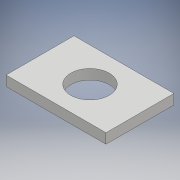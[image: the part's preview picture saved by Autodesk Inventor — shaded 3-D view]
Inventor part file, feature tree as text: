
AUTODESK INVENTOR PART (.ipt)
format: ipt  version: 2018 (Build 220112000, 112)  size: 101,376 bytes
history: native  units: mm
features: other x1, extrude x1, sketch x1
ambient origin geometry x8: Origin, YZ Plane, XZ Plane, XY Plane, X Axis, Y Axis, Z Axis, Center Point
bodies: Body1 (feature_tree)
feature tree (3):
  other  "ソリッド1"
  extrude  "押し出し1"  Depth=40.0mm
  sketch  "スケッチ1"
